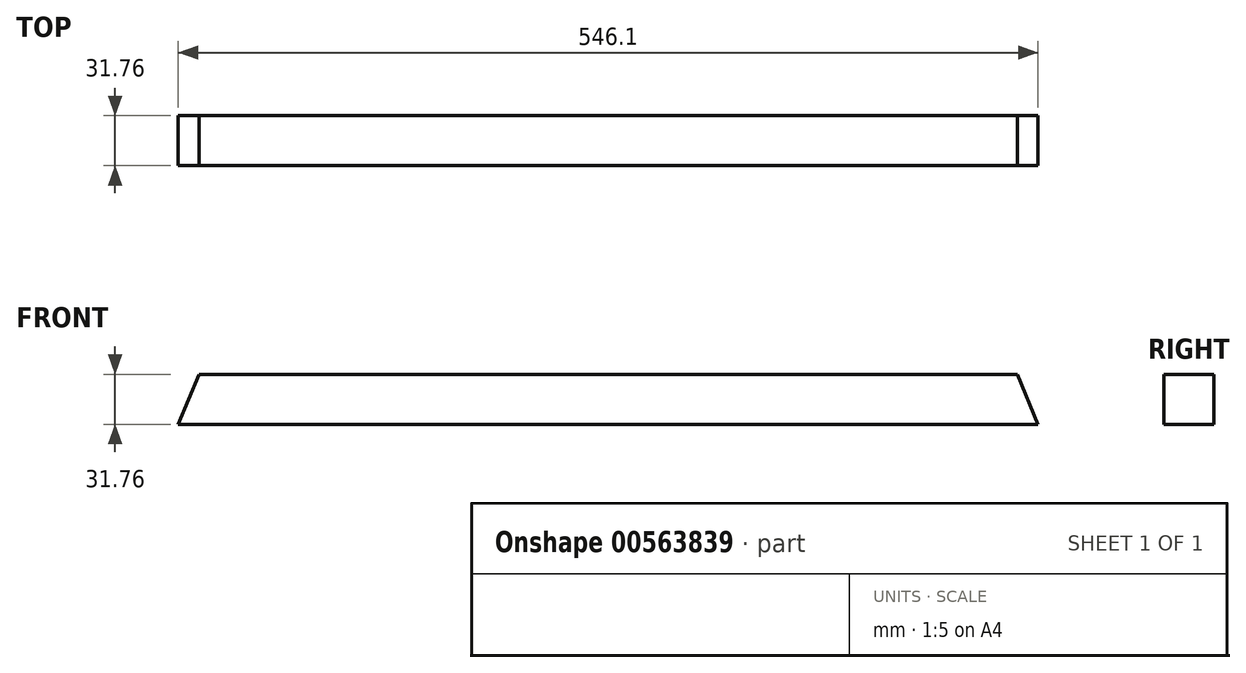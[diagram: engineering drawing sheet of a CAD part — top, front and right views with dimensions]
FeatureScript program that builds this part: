
annotation { "Feature Type Name" : "Feature", "Feature Type Description" : "" }
export const myFeature = defineFeature(function(context is Context, id is Id, definition is map)
    precondition{}
    {
        {
            var Q0;
            Q0=qCreatedBy(makeId("Front.planeOp"),FACE);
            var sketch = newSketch(context, id + "F0", { "sketchPlane" : qUnion([Q0])});
            skLineSegment(sketch, "E0.bottom", {"start": v(-273.05, 15.88) * mm, "end": v(273.05, 15.88) * mm});
            skLineSegment(sketch, "E0.top", {"start": v(-273.05, -15.88) * mm, "end": v(273.05, -15.88) * mm});
            skLineSegment(sketch, "E0.left", {"start": v(-273.05, 15.88) * mm, "end": v(-273.05, -15.88) * mm});
            skLineSegment(sketch, "E0.right", {"start": v(273.05, 15.88) * mm, "end": v(273.05, -15.88) * mm});
            skPoint(sketch, "E0.middle", {"position": v(0, 0) * mm});
            skLineSegment(sketch, "E1", {"start": v(-273.05, -15.87) * mm, "end": v(-259.9, 15.88) * mm});
            skLineSegment(sketch, "E2", {"start": v(273.05, -15.88) * mm, "end": v(259.9, 15.87) * mm});
            skSolve(sketch);
        }
        {
            var Q0;
            Q0=makeQuery(id+"F0.imprint","IMPRINT",FACE,{"disambiguationData":[TD([[makeQuery(id+"F0.imprint","IMPRINT",EDGE,{"derivedFrom":sQuery(id+"F0.wireOp",EDGE,"E0.top")}),1.0]])]});
            extrude(context, id + "F1", {"entities" : qUnion([Q0]), "endBound" : BoundingType.SYMMETRIC, "depth" : 31.75 * mm, "offsetDistance" : 25.4 * mm});
        }
    });
